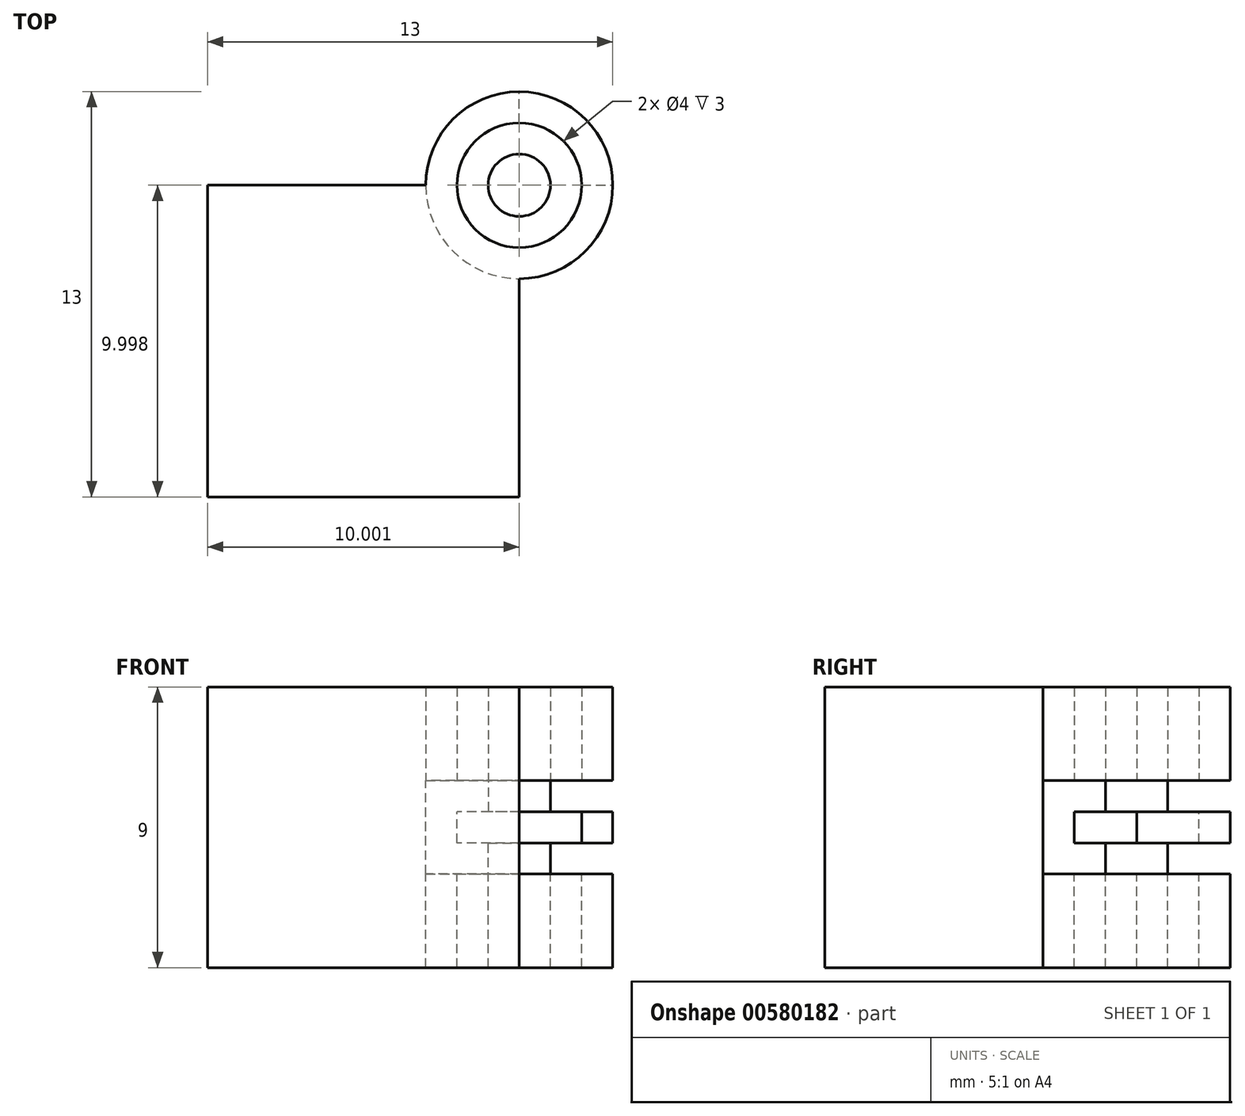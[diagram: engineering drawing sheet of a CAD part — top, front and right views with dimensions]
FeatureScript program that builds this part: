
annotation { "Feature Type Name" : "Feature", "Feature Type Description" : "" }
export const myFeature = defineFeature(function(context is Context, id is Id, definition is map)
    precondition{}
    {
        {
            var Q0;
            Q0=qCreatedBy(makeId("Top.planeOp"),FACE);
            var sketch = newSketch(context, id + "F0", { "sketchPlane" : qUnion([Q0])});
            skLineSegment(sketch, "E0.bottom", {"start": v(-56, 31.3) * mm, "end": v(-46, 31.3) * mm});
            skLineSegment(sketch, "E0.top", {"start": v(-56, 21.3) * mm, "end": v(-46, 21.3) * mm});
            skLineSegment(sketch, "E0.left", {"start": v(-56, 31.3) * mm, "end": v(-56, 21.3) * mm});
            skLineSegment(sketch, "E0.right", {"start": v(-46, 31.3) * mm, "end": v(-46, 21.3) * mm});
            skCircle(sketch, "E1", {"center": v(-46, 31.3) * mm, "radius": 3 * mm});
            skCircle(sketch, "E2", {"center": v(-46, 31.3) * mm, "radius": 2 * mm});
            skCircle(sketch, "E3", {"center": v(-46, 31.3) * mm, "radius": 1 * mm});
            skSolve(sketch);
        }
        {
            var Q0;
            {var subQ1=sQuery(id+"F0.wireOp",EDGE,"E0.top");Q0=makeQuery(id+"F0.imprint","IMPRINT",FACE,{"disambiguationData":[TD([[makeQuery(id+"F0.imprint","IMPRINT",EDGE,{"derivedFrom":subQ1}),1.0]])]});}
            var Q1;
            {var subQ0=sQuery(id+"F0.wireOp",EDGE,"E1");var subQ1=sQuery(id+"F0.wireOp",EDGE,"E0.bottom");var subQ2=makeQuery(id+"F0.imprint","INTERSECT",VERTEX,{"derivedFrom":[subQ1,subQ0]});Q1=makeQuery(id+"F0.imprint","IMPRINT",FACE,{"disambiguationData":[TD([[makeQuery(id+"F0.imprint","IMPRINT",EDGE,{"disambiguationData":[TD([[subQ2,-1.0]])],"derivedFrom":subQ1}),1.0]])]});}
            var Q2;
            {var subQ0=sQuery(id+"F0.wireOp",EDGE,"E0.right");var subQ1=sQuery(id+"F0.wireOp",EDGE,"E0.bottom");var subQ2=makeQuery(id+"F0.imprint","INTERSECT",VERTEX,{"derivedFrom":[subQ1,subQ0]});Q2=makeQuery(id+"F0.imprint","IMPRINT",FACE,{"disambiguationData":[TD([[makeQuery(id+"F0.imprint","IMPRINT",EDGE,{"disambiguationData":[TD([[subQ2,1.0]])],"derivedFrom":subQ1}),-1.0]])]});}
            var Q3;
            {var subQ0=sQuery(id+"F0.wireOp",EDGE,"E0.right");var subQ1=sQuery(id+"F0.wireOp",EDGE,"E0.bottom");var subQ2=makeQuery(id+"F0.imprint","INTERSECT",VERTEX,{"derivedFrom":[subQ1,subQ0]});Q3=makeQuery(id+"F0.imprint","IMPRINT",FACE,{"disambiguationData":[TD([[makeQuery(id+"F0.imprint","IMPRINT",EDGE,{"disambiguationData":[TD([[subQ2,1.0]])],"derivedFrom":subQ1}),1.0]])]});}
            var Q4;
            {var subQ0=sQuery(id+"F0.wireOp",EDGE,"E1");var subQ1=sQuery(id+"F0.wireOp",EDGE,"E0.bottom");var subQ2=makeQuery(id+"F0.imprint","INTERSECT",VERTEX,{"derivedFrom":[subQ1,subQ0]});Q4=makeQuery(id+"F0.imprint","IMPRINT",FACE,{"disambiguationData":[TD([[makeQuery(id+"F0.imprint","IMPRINT",EDGE,{"disambiguationData":[TD([[subQ2,-1.0]])],"derivedFrom":subQ1}),-1.0]])]});}
            extrude(context, id + "F1", {"entities" : qUnion([Q0, Q1, Q2, Q3, Q4]), "depth" : 3 * mm, "offsetDistance" : 25 * mm});
        }
        {
            var Q0;
            {var subQ1=sQuery(id+"F0.wireOp",EDGE,"E0.top");Q0=makeQuery(id+"F0.imprint","IMPRINT",FACE,{"disambiguationData":[TD([[makeQuery(id+"F0.imprint","IMPRINT",EDGE,{"derivedFrom":subQ1}),1.0]])]});}
            extrude(context, id + "F2", {"entities" : qUnion([Q0]), "operationType" : NewBodyOperationType.ADD, "oppositeDirection" : true, "depth" : 1 * mm, "offsetDistance" : 25 * mm});
        }
        {
            var Q0;
            {var subQ0=sQuery(id+"F0.wireOp",EDGE,"E0.right");var subQ1=sQuery(id+"F0.wireOp",EDGE,"E0.bottom");var subQ2=makeQuery(id+"F0.imprint","INTERSECT",VERTEX,{"derivedFrom":[subQ1,subQ0]});Q0=makeQuery(id+"F0.imprint","IMPRINT",FACE,{"disambiguationData":[TD([[makeQuery(id+"F0.imprint","IMPRINT",EDGE,{"disambiguationData":[TD([[subQ2,1.0]])],"derivedFrom":subQ1}),-1.0]])]});}
            var Q1;
            {var subQ0=sQuery(id+"F0.wireOp",EDGE,"E0.right");var subQ1=sQuery(id+"F0.wireOp",EDGE,"E0.bottom");var subQ2=makeQuery(id+"F0.imprint","INTERSECT",VERTEX,{"derivedFrom":[subQ1,subQ0]});Q1=makeQuery(id+"F0.imprint","IMPRINT",FACE,{"disambiguationData":[TD([[makeQuery(id+"F0.imprint","IMPRINT",EDGE,{"disambiguationData":[TD([[subQ2,1.0]])],"derivedFrom":subQ1}),1.0]])]});}
            extrude(context, id + "F3", {"entities" : qUnion([Q0, Q1]), "operationType" : NewBodyOperationType.ADD, "oppositeDirection" : true, "depth" : 1 * mm, "offsetDistance" : 25 * mm});
        }
        {
            var Q0;
            Q0=makeQuery(id+"F2.opExtrude","CAP_FACE",FACE,{"disambiguationData":[OSD([sQuery(id+"F0.wireOp",EDGE,"E0.bottom"),sQuery(id+"F0.wireOp",EDGE,"E0.top"),sQuery(id+"F0.wireOp",EDGE,"E0.left"),sQuery(id+"F0.wireOp",EDGE,"E0.right"),sQuery(id+"F0.wireOp",EDGE,"E1")])],"isStart":false});
            var sketch = newSketch(context, id + "F4", { "sketchPlane" : qUnion([Q0])});
            skLineSegment(sketch, "E4.0", {"start": v(-46, -28.3) * mm, "end": v(-46, -21.3) * mm});
            skArc(sketch, "E4.1", {"start": v(-49, -31.3) * mm, "mid": v(-48.12, -29.18) * mm, "end": v(-46, -28.3) * mm});
            skLineSegment(sketch, "E4.2", {"start": v(-46, -21.3) * mm, "end": v(-56, -21.3) * mm});
            skLineSegment(sketch, "E4.3", {"start": v(-56, -21.3) * mm, "end": v(-56, -31.3) * mm});
            skLineSegment(sketch, "E4.4", {"start": v(-56, -31.3) * mm, "end": v(-49, -31.3) * mm});
            skArc(sketch, "E5.0", {"start": v(-46, -28.3) * mm, "mid": v(-48.12, -29.18) * mm, "end": v(-49, -31.3) * mm});
            skArc(sketch, "E5.1", {"start": v(-49, -31.3) * mm, "mid": v(-43.88, -33.42) * mm, "end": v(-46, -28.3) * mm});
            skCircle(sketch, "E6.0", {"center": v(-46, -31.3) * mm, "radius": 2 * mm});
            skCircle(sketch, "E7.0", {"center": v(-46, -31.3) * mm, "radius": 1 * mm});
            skLineSegment(sketch, "E8", {"start": v(-46, -31.3) * mm, "end": v(-46, -34.3) * mm});
            skLineSegment(sketch, "E9", {"start": v(-46, -31.3) * mm, "end": v(-43, -31.3) * mm});
            skSolve(sketch);
        }
        {
            var Q0;
            Q0=makeQuery(id+"F4.imprint","IMPRINT",FACE,{"disambiguationData":[TD([[makeQuery(id+"F4.imprint","IMPRINT",EDGE,{"derivedFrom":sQuery(id+"F4.wireOp",EDGE,"E4.0")}),1.0]])]});
            extrude(context, id + "F5", {"entities" : qUnion([Q0]), "operationType" : NewBodyOperationType.ADD, "depth" : 1 * mm, "offsetDistance" : 25 * mm});
        }
        {
            var Q0;
            {var subQ0=sQuery(id+"F4.wireOp",EDGE,"E8");var subQ1=sQuery(id+"F4.wireOp",EDGE,"E7.0");var subQ2=makeQuery(id+"F4.imprint","INTERSECT",VERTEX,{"derivedFrom":[subQ1,subQ0]});Q0=makeQuery(id+"F4.imprint","IMPRINT",FACE,{"disambiguationData":[TD([[makeQuery(id+"F4.imprint","IMPRINT",EDGE,{"disambiguationData":[TD([[subQ2,1.0]])],"derivedFrom":subQ1}),1.0]])]});}
            var Q1;
            {var subQ0=sQuery(id+"F4.wireOp",EDGE,"E8");var subQ1=sQuery(id+"F4.wireOp",EDGE,"E6.0");var subQ2=makeQuery(id+"F4.imprint","INTERSECT",VERTEX,{"derivedFrom":[subQ1,subQ0]});Q1=makeQuery(id+"F4.imprint","IMPRINT",FACE,{"disambiguationData":[TD([[makeQuery(id+"F4.imprint","IMPRINT",EDGE,{"disambiguationData":[TD([[subQ2,1.0]])],"derivedFrom":subQ1}),1.0]])]});}
            var Q2;
            {var subQ0=sQuery(id+"F4.wireOp",EDGE,"E8");var subQ1=sQuery(id+"F4.wireOp",EDGE,"E6.0");var subQ2=makeQuery(id+"F4.imprint","INTERSECT",VERTEX,{"derivedFrom":[subQ1,subQ0]});Q2=makeQuery(id+"F4.imprint","IMPRINT",FACE,{"disambiguationData":[TD([[makeQuery(id+"F4.imprint","IMPRINT",EDGE,{"disambiguationData":[TD([[subQ2,-1.0]])],"derivedFrom":subQ1}),1.0]])]});}
            var Q3;
            {var subQ0=sQuery(id+"F4.wireOp",EDGE,"E8");var subQ1=sQuery(id+"F4.wireOp",EDGE,"E5.1");var subQ2=makeQuery(id+"F4.imprint","INTERSECT",VERTEX,{"derivedFrom":[subQ1,subQ0]});Q3=makeQuery(id+"F4.imprint","IMPRINT",FACE,{"disambiguationData":[TD([[makeQuery(id+"F4.imprint","IMPRINT",EDGE,{"disambiguationData":[TD([[subQ2,-1.0]])],"derivedFrom":subQ1}),1.0]])]});}
            var Q4;
            {var subQ0=sQuery(id+"F4.wireOp",EDGE,"E8");var subQ1=sQuery(id+"F4.wireOp",EDGE,"E7.0");var subQ2=makeQuery(id+"F4.imprint","INTERSECT",VERTEX,{"derivedFrom":[subQ1,subQ0]});Q4=makeQuery(id+"F4.imprint","IMPRINT",FACE,{"disambiguationData":[TD([[makeQuery(id+"F4.imprint","IMPRINT",EDGE,{"disambiguationData":[TD([[subQ2,-1.0]])],"derivedFrom":subQ1}),1.0]])]});}
            extrude(context, id + "F6", {"entities" : qUnion([Q0, Q1, Q2, Q3, Q4]), "operationType" : NewBodyOperationType.ADD, "depth" : 1 * mm, "offsetDistance" : 25 * mm});
        }
        {
            var Q0;
            Q0=makeQuery(id+"F5.opExtrude","CAP_FACE",FACE,{"disambiguationData":[OSD([sQuery(id+"F4.wireOp",EDGE,"E4.0"),sQuery(id+"F4.wireOp",EDGE,"E4.2"),sQuery(id+"F4.wireOp",EDGE,"E4.3"),sQuery(id+"F4.wireOp",EDGE,"E4.4"),sQuery(id+"F4.wireOp",EDGE,"E5.0")])],"isStart":false});
            var sketch = newSketch(context, id + "F7", { "sketchPlane" : qUnion([Q0])});
            skArc(sketch, "E10.0", {"start": v(-49, -31.3) * mm, "mid": v(-48.12, -29.18) * mm, "end": v(-46, -28.3) * mm});
            skLineSegment(sketch, "E10.1", {"start": v(-56, -31.3) * mm, "end": v(-49, -31.3) * mm});
            skLineSegment(sketch, "E10.2", {"start": v(-46, -28.3) * mm, "end": v(-46, -21.3) * mm});
            skLineSegment(sketch, "E10.3", {"start": v(-46, -21.3) * mm, "end": v(-56, -21.3) * mm});
            skLineSegment(sketch, "E10.4", {"start": v(-56, -21.3) * mm, "end": v(-56, -31.3) * mm});
            skCircle(sketch, "E11.0", {"center": v(-46, -31.3) * mm, "radius": 1 * mm});
            skSolve(sketch);
        }
        {
            var Q0;
            Q0=makeQuery(id+"F7.imprint","IMPRINT",FACE,{"disambiguationData":[TD([[makeQuery(id+"F7.imprint","IMPRINT",EDGE,{"derivedFrom":sQuery(id+"F7.wireOp",EDGE,"E10.0")}),1.0]])]});
            extrude(context, id + "F8", {"entities" : qUnion([Q0]), "operationType" : NewBodyOperationType.ADD, "depth" : 1 * mm, "offsetDistance" : 25 * mm});
        }
        {
            var Q0;
            Q0=makeQuery(id+"F7.imprint","IMPRINT",FACE,{"disambiguationData":[TD([[makeQuery(id+"F7.imprint","IMPRINT",EDGE,{"derivedFrom":sQuery(id+"F7.wireOp",EDGE,"E11.0")}),1.0]])]});
            extrude(context, id + "F9", {"entities" : qUnion([Q0]), "operationType" : NewBodyOperationType.ADD, "depth" : 1 * mm, "offsetDistance" : 25 * mm});
        }
        {
            var Q0;
            Q0=makeQuery(id+"F8.opExtrude","CAP_FACE",FACE,{"disambiguationData":[OSD([sQuery(id+"F7.wireOp",EDGE,"E10.0"),sQuery(id+"F7.wireOp",EDGE,"E10.1"),sQuery(id+"F7.wireOp",EDGE,"E10.2"),sQuery(id+"F7.wireOp",EDGE,"E10.3"),sQuery(id+"F7.wireOp",EDGE,"E10.4")])],"isStart":false});
            var sketch = newSketch(context, id + "F10", { "sketchPlane" : qUnion([Q0])});
            skLineSegment(sketch, "E12.0", {"start": v(-56, -31.3) * mm, "end": v(-49, -31.3) * mm});
            skLineSegment(sketch, "E12.1", {"start": v(-56, -21.3) * mm, "end": v(-56, -31.3) * mm});
            skArc(sketch, "E12.2", {"start": v(-49, -31.3) * mm, "mid": v(-48.12, -29.18) * mm, "end": v(-46, -28.3) * mm});
            skLineSegment(sketch, "E12.3", {"start": v(-46, -28.3) * mm, "end": v(-46, -21.3) * mm});
            skLineSegment(sketch, "E12.4", {"start": v(-46, -21.3) * mm, "end": v(-56, -21.3) * mm});
            skSolve(sketch);
        }
        {
            var Q0;
            Q0=makeQuery(id+"F10.imprint","IMPRINT",FACE,{"disambiguationData":[TD([[makeQuery(id+"F10.imprint","IMPRINT",EDGE,{"derivedFrom":sQuery(id+"F10.wireOp",EDGE,"E12.0")}),1.0]])]});
            extrude(context, id + "F11", {"entities" : qUnion([Q0]), "operationType" : NewBodyOperationType.ADD, "depth" : 3 * mm, "offsetDistance" : 25 * mm});
        }
        {
            var Q0;
            Q0=makeQuery(id+"F9.opExtrude","CAP_FACE",FACE,{"disambiguationData":[OSD([sQuery(id+"F7.wireOp",EDGE,"E11.0")])],"isStart":false});
            var sketch = newSketch(context, id + "F12", { "sketchPlane" : qUnion([Q0])});
            skArc(sketch, "E13.0", {"start": v(-46, -28.3) * mm, "mid": v(-48.12, -29.18) * mm, "end": v(-49, -31.3) * mm});
            skArc(sketch, "E13.1", {"start": v(-49, -31.3) * mm, "mid": v(-43.88, -33.42) * mm, "end": v(-46, -28.3) * mm});
            skCircle(sketch, "E14.0", {"center": v(-46, -31.3) * mm, "radius": 2 * mm});
            skSolve(sketch);
        }
        {
            var Q0;
            Q0=makeQuery(id+"F12.imprint","IMPRINT",FACE,{"disambiguationData":[TD([[makeQuery(id+"F12.imprint","IMPRINT",EDGE,{"derivedFrom":sQuery(id+"F12.wireOp",EDGE,"E13.0")}),1.0]])]});
            var Q1;
            Q1=makeQuery(id+"F11.opExtrude","CAP_FACE",FACE,{"disambiguationData":[OSD([sQuery(id+"F10.wireOp",EDGE,"E12.0"),sQuery(id+"F10.wireOp",EDGE,"E12.1"),sQuery(id+"F10.wireOp",EDGE,"E12.2"),sQuery(id+"F10.wireOp",EDGE,"E12.3"),sQuery(id+"F10.wireOp",EDGE,"E12.4")])],"isStart":false});
            extrude(context, id + "F13", {"entities" : qUnion([Q0]), "operationType" : NewBodyOperationType.ADD, "endBound" : BoundingType.UP_TO_SURFACE, "depth" : 25 * mm, "endBoundEntityFace" : qUnion([Q1]), "offsetDistance" : 25 * mm});
        }
        {
            var Q0;
            Q0=makeQuery(id+"F9.opExtrude","CAP_FACE",FACE,{"disambiguationData":[OSD([sQuery(id+"F7.wireOp",EDGE,"E11.0")])],"isStart":false});
            var Q1;
            {var subQ0=sQuery(id+"F10.wireOp",EDGE,"E12.4");var subQ1=sQuery(id+"F10.wireOp",EDGE,"E12.3");var subQ2=sQuery(id+"F10.wireOp",EDGE,"E12.2");var subQ3=sQuery(id+"F10.wireOp",EDGE,"E12.1");var subQ4=sQuery(id+"F10.wireOp",EDGE,"E12.0");Q1=makeQuery(id+"F13.boolean.opBoolean","MERGE",FACE,{"derivedFrom":[makeQuery(id+"F11.opExtrude","CAP_FACE",FACE,{"disambiguationData":[OSD([subQ4,subQ3,subQ2,subQ1,subQ0])],"isStart":false}),makeQuery(id+"F13.opExtrude","CAP_FACE",FACE,{"disambiguationData":[OSD([subQ4,subQ3,subQ2,subQ1,subQ0])],"isStart":false})]});}
            extrude(context, id + "F14", {"entities" : qUnion([Q0]), "operationType" : NewBodyOperationType.ADD, "endBound" : BoundingType.UP_TO_SURFACE, "depth" : 25 * mm, "endBoundEntityFace" : qUnion([Q1]), "offsetDistance" : 25 * mm});
        }
    });
